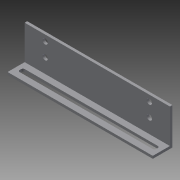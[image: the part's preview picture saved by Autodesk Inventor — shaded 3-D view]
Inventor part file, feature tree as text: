
AUTODESK INVENTOR PART (.ipt)
format: ipt  version: 2015 (Build 190159000, 159)  size: 185,344 bytes
history: native  units: mm
features: sketch x9, extrude x7, hole x2, other x1, fillet x1
ambient origin geometry x8: Origin, YZ Plane, XZ Plane, XY Plane, X Axis, Y Axis, Z Axis, Center Point
bodies: Body1 (feature_tree), Body2 (feature_tree)
feature tree (20):
  other  "ソリッド1"
  extrude  "押し出し1"  Depth=45.0mm
  extrude  "押し出し2"  Depth=177.5mm
  hole  "穴1"  [1 undecoded]
  extrude  "押し出し3"  Depth=25.0mm
  extrude  "押し出し4"  Depth=167.5mm
  extrude  "押し出し5"  Depth=1.5mm TaperAngle=0.0deg
  fillet  "フィレット1"  [1 undecoded]
  extrude  "押し出し6"  Depth=5.0mm
  extrude  "押し出し7"  Depth=5.0mm
  hole  "穴2"  [1 undecoded]
  sketch  "スケッチ1"
  sketch  "スケッチ2"
  sketch  "スケッチ3"
  sketch  "スケッチ4"
  sketch  "スケッチ5"
  sketch  "スケッチ6"
  sketch  "スケッチ7"
  sketch  "スケッチ8"
  sketch  "スケッチ10"
note: 3 required parameter values undecoded (feature->parameter linkage not recoverable at this tier; creation-order binding heuristic only, values carry confidence <= 0.55)
